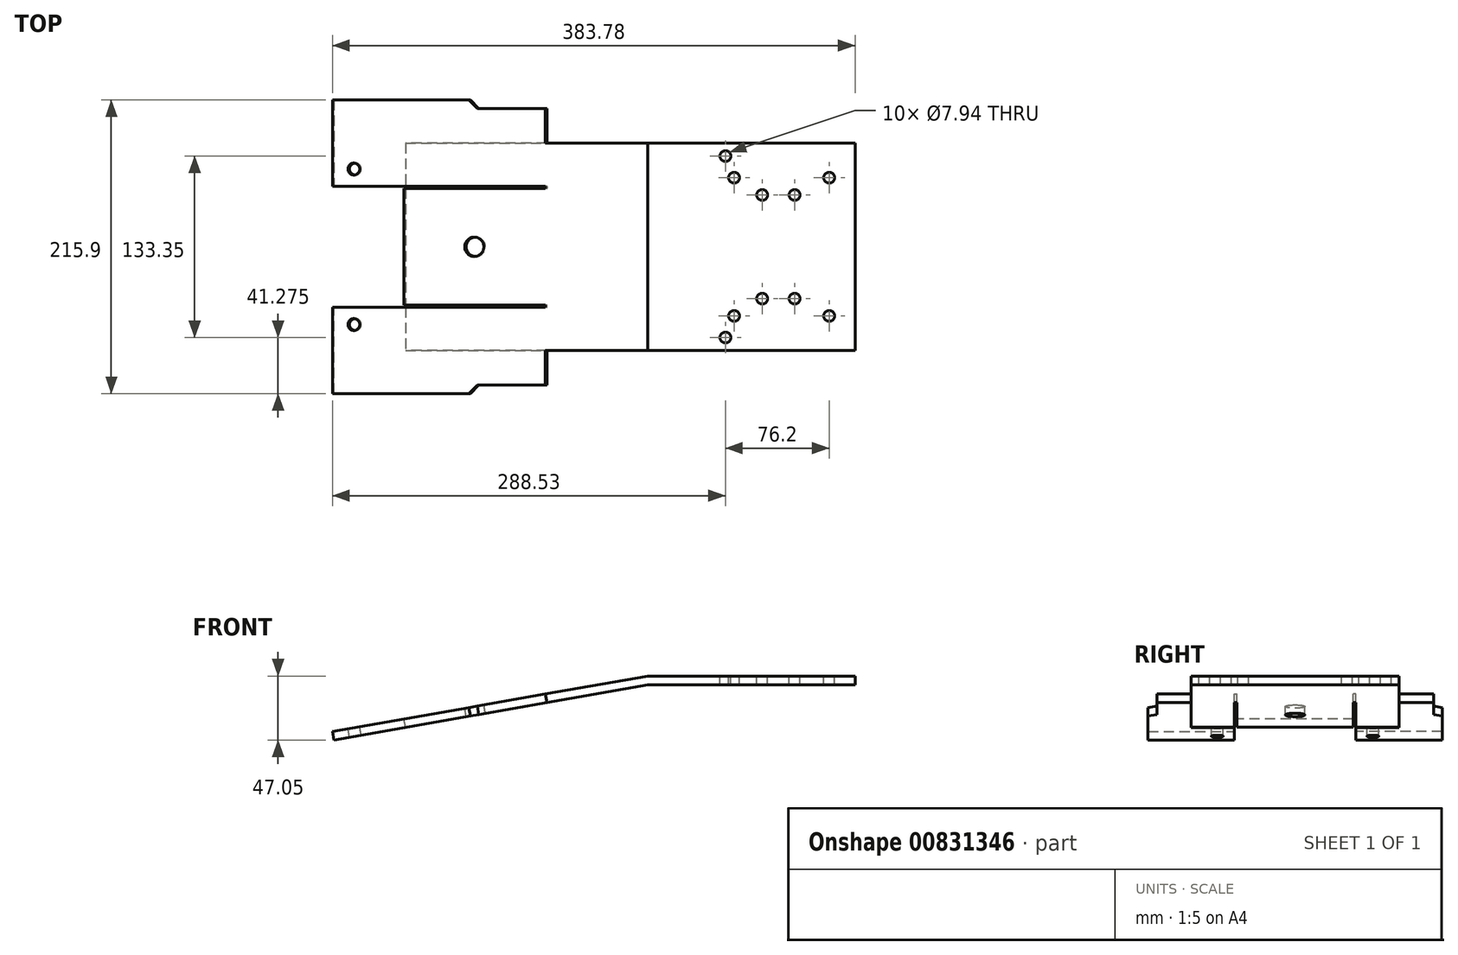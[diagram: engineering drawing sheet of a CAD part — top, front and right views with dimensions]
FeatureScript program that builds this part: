
annotation { "Feature Type Name" : "Feature", "Feature Type Description" : "" }
export const myFeature = defineFeature(function(context is Context, id is Id, definition is map)
    precondition{}
    {
        {
            var Q0;
            Q0=qCreatedBy(makeId("Front.planeOp"),FACE);
            var sketch = newSketch(context, id + "F0", { "sketchPlane" : qUnion([Q0])});
            skLineSegment(sketch, "E0", {"start": v(0, 0) * mm, "end": v(-152.4, 0) * mm});
            skLineSegment(sketch, "E1", {"start": v(-152.4, 0) * mm, "end": v(-330.2, -31.35) * mm});
            skLineSegment(sketch, "E2", {"start": v(-330.2, -31.35) * mm, "end": v(-331.29, -25.2) * mm});
            skLineSegment(sketch, "E3", {"start": v(-331.29, -25.2) * mm, "end": v(-152.4, 6.35) * mm});
            skLineSegment(sketch, "E4", {"start": v(-152.4, 6.35) * mm, "end": v(0, 6.35) * mm});
            skLineSegment(sketch, "E5", {"start": v(0, 6.35) * mm, "end": v(0, 0) * mm});
            skSolve(sketch);
        }
        {
            var Q0;
            Q0 = qSketchRegion(id + "F0", true);
            extrude(context, id + "F1", {"entities" : qUnion([Q0]), "oppositeDirection" : true, "depth" : 152.4 * mm, "offsetDistance" : 25.4 * mm});
        }
        {
            var Q0;
            Q0=makeQuery(id+"F1.opExtrude","SWEPT_FACE",FACE,{"disambiguationData":[OSD([sQuery(id+"F0.wireOp",EDGE,"E3")])]});
            var sketch = newSketch(context, id + "F2", { "sketchPlane" : qUnion([Q0])});
            skCircle(sketch, "E6", {"center": v(-278.24, 76.2) * mm, "radius": 7.14 * mm});
            skPoint(sketch, "E6.centerSnap0", {"position": v(-330.63, 76.2) * mm});
            skSolve(sketch);
        }
        {
            var Q0;
            Q0 = qSketchRegion(id + "F2", true);
            extrude(context, id + "F3", {"entities" : qUnion([Q0]), "operationType" : NewBodyOperationType.REMOVE, "endBound" : BoundingType.THROUGH_ALL, "oppositeDirection" : true, "depth" : 25.4 * mm, "offsetDistance" : 25.4 * mm});
        }
        {
            var Q0;
            Q0=makeQuery(id+"F1.opExtrude","SWEPT_FACE",FACE,{"disambiguationData":[OSD([sQuery(id+"F0.wireOp",EDGE,"E4")])]});
            var sketch = newSketch(context, id + "F4", { "sketchPlane" : qUnion([Q0])});
            skCircle(sketch, "E7", {"center": v(-19.05, 127) * mm, "radius": 3.97 * mm});
            skCircle(sketch, "E8", {"center": v(-19.05, 25.4) * mm, "radius": 3.97 * mm});
            skCircle(sketch, "E9", {"center": v(-88.9, 25.4) * mm, "radius": 3.97 * mm});
            skCircle(sketch, "E10", {"center": v(-88.9, 127) * mm, "radius": 3.97 * mm});
            skCircle(sketch, "E11", {"center": v(-95.25, 9.53) * mm, "radius": 3.97 * mm});
            skCircle(sketch, "E12", {"center": v(-95.25, 142.88) * mm, "radius": 3.97 * mm});
            skCircle(sketch, "E13", {"center": v(-68.26, 114.3) * mm, "radius": 3.97 * mm});
            skCircle(sketch, "E14", {"center": v(-44.45, 114.3) * mm, "radius": 3.97 * mm});
            skCircle(sketch, "E15", {"center": v(-68.26, 38.1) * mm, "radius": 3.97 * mm});
            skCircle(sketch, "E16", {"center": v(-44.45, 38.1) * mm, "radius": 3.97 * mm});
            skSolve(sketch);
        }
        {
            var Q0;
            Q0 = qSketchRegion(id + "F4", true);
            extrude(context, id + "F5", {"entities" : qUnion([Q0]), "operationType" : NewBodyOperationType.REMOVE, "endBound" : BoundingType.THROUGH_ALL, "oppositeDirection" : true, "depth" : 25.4 * mm, "offsetDistance" : 25.4 * mm});
        }
        {
            var Q0;
            Q0=makeQuery(id+"F1.opExtrude","SWEPT_FACE",FACE,{"disambiguationData":[OSD([sQuery(id+"F0.wireOp",EDGE,"E3")])]});
            var sketch = newSketch(context, id + "F6", { "sketchPlane" : qUnion([Q0])});
            skLineSegment(sketch, "E17.0", {"start": v(-330.63, 152.4) * mm, "end": v(-225.18, 152.4) * mm});
            skLineSegment(sketch, "E17.1", {"start": v(-330.63, 152.4) * mm, "end": v(-330.63, 120.65) * mm});
            skLineSegment(sketch, "E18.0", {"start": v(-383.93, 184.15) * mm, "end": v(-282.33, 184.15) * mm});
            skLineSegment(sketch, "E19.0", {"start": v(-383.93, 120.65) * mm, "end": v(-330.63, 120.65) * mm});
            skLineSegment(sketch, "E20.0", {"start": v(-148.98, 152.4) * mm, "end": v(-148.98, 0) * mm});
            skLineSegment(sketch, "E21.0", {"start": v(-225.18, 177.8) * mm, "end": v(-225.18, 152.4) * mm});
            skLineSegment(sketch, "E22.0", {"start": v(-383.93, 184.15) * mm, "end": v(-383.93, 120.65) * mm});
            skLineSegment(sketch, "E23.0", {"start": v(-275.98, 177.8) * mm, "end": v(-225.18, 177.8) * mm});
            skLineSegment(sketch, "E24", {"start": v(-282.33, 184.15) * mm, "end": v(-275.98, 177.8) * mm});
            skLineSegment(sketch, "E25", {"start": v(-278.24, 76.2) * mm, "end": v(-330.63, 76.2) * mm});
            skLineSegment(sketch, "E26.MirrorCS", {"start": v(-282.33, -31.75) * mm, "end": v(-275.98, -25.4) * mm});
            skLineSegment(sketch, "E27.MirrorCS", {"start": v(-383.93, 31.75) * mm, "end": v(-330.63, 31.75) * mm});
            skLineSegment(sketch, "E28.MirrorCS", {"start": v(-225.18, -25.4) * mm, "end": v(-225.18, 0) * mm});
            skLineSegment(sketch, "E29.MirrorCS", {"start": v(-275.98, -25.4) * mm, "end": v(-225.18, -25.4) * mm});
            skLineSegment(sketch, "E30.MirrorCS", {"start": v(-330.63, 0) * mm, "end": v(-330.63, 31.75) * mm});
            skLineSegment(sketch, "E31.MirrorCS", {"start": v(-383.93, -31.75) * mm, "end": v(-383.93, 31.75) * mm});
            skLineSegment(sketch, "E32.MirrorCS", {"start": v(-383.93, -31.75) * mm, "end": v(-282.33, -31.75) * mm});
            skLineSegment(sketch, "E33.MirrorCS", {"start": v(-330.63, 0) * mm, "end": v(-225.18, 0) * mm});
            skSolve(sketch);
        }
        {
            var Q0;
            Q0 = qSketchRegion(id + "F6", true);
            extrude(context, id + "F7", {"entities" : qUnion([Q0]), "operationType" : NewBodyOperationType.ADD, "oppositeDirection" : true, "depth" : 6.35 * mm, "offsetDistance" : 25.4 * mm});
        }
        {
            var Q0;
            Q0=makeQuery(id+"F7.boolean.opBoolean","MERGE",FACE,{"derivedFrom":[makeQuery(id+"F1.opExtrude","SWEPT_FACE",FACE,{"disambiguationData":[OSD([sQuery(id+"F0.wireOp",EDGE,"E3")])]}),makeQuery(id+"F7.opExtrude","CAP_FACE",FACE,{"disambiguationData":[OSD([sQuery(id+"F6.wireOp",EDGE,"E17.0"),sQuery(id+"F6.wireOp",EDGE,"E17.1"),sQuery(id+"F6.wireOp",EDGE,"E18.0"),sQuery(id+"F6.wireOp",EDGE,"E19.0"),sQuery(id+"F6.wireOp",EDGE,"E21.0"),sQuery(id+"F6.wireOp",EDGE,"E22.0"),sQuery(id+"F6.wireOp",EDGE,"E23.0"),sQuery(id+"F6.wireOp",EDGE,"E24")])],"isStart":true}),makeQuery(id+"F7.opExtrude","CAP_FACE",FACE,{"disambiguationData":[OSD([sQuery(id+"F6.wireOp",EDGE,"E26.MirrorCS"),sQuery(id+"F6.wireOp",EDGE,"E27.MirrorCS"),sQuery(id+"F6.wireOp",EDGE,"E28.MirrorCS"),sQuery(id+"F6.wireOp",EDGE,"E29.MirrorCS"),sQuery(id+"F6.wireOp",EDGE,"E30.MirrorCS"),sQuery(id+"F6.wireOp",EDGE,"E31.MirrorCS"),sQuery(id+"F6.wireOp",EDGE,"E32.MirrorCS"),sQuery(id+"F6.wireOp",EDGE,"E33.MirrorCS")])],"isStart":true})]});
            var sketch = newSketch(context, id + "F8", { "sketchPlane" : qUnion([Q0])});
            skPoint(sketch, "E34.endSnap0", {"position": v(-357.28, 31.75) * mm});
            skLineSegment(sketch, "E35.0", {"start": v(-383.93, 184.15) * mm, "end": v(-383.93, 120.65) * mm});
            skLineSegment(sketch, "E35.3", {"start": v(-383.93, -31.75) * mm, "end": v(-383.93, 31.75) * mm});
            skCircle(sketch, "E36", {"center": v(-368.06, 133.35) * mm, "radius": 4.37 * mm});
            skCircle(sketch, "E37", {"center": v(-368.06, 19.05) * mm, "radius": 4.37 * mm});
            skLineSegment(sketch, "E38", {"start": v(-383.93, 120.65) * mm, "end": v(-225.18, 120.65) * mm});
            skLineSegment(sketch, "E39", {"start": v(-383.93, 31.75) * mm, "end": v(-225.18, 31.75) * mm});
            skLineSegment(sketch, "E40.0", {"start": v(-383.93, 119.06) * mm, "end": v(-225.18, 119.06) * mm});
            skLineSegment(sketch, "E41.0", {"start": v(-383.93, 33.34) * mm, "end": v(-225.18, 33.34) * mm});
            skLineSegment(sketch, "E42", {"start": v(-225.18, 120.65) * mm, "end": v(-225.18, 119.06) * mm});
            skLineSegment(sketch, "E43", {"start": v(-225.18, 31.75) * mm, "end": v(-225.18, 33.34) * mm});
            skLineSegment(sketch, "E44", {"start": v(-330.63, 120.65) * mm, "end": v(-330.63, 119.06) * mm});
            skLineSegment(sketch, "E45", {"start": v(-330.63, 31.75) * mm, "end": v(-330.63, 33.34) * mm});
            skSolve(sketch);
        }
        {
            var Q0;
            Q0 = qSketchRegion(id + "F8", true);
            extrude(context, id + "F9", {"entities" : qUnion([Q0]), "operationType" : NewBodyOperationType.REMOVE, "endBound" : BoundingType.THROUGH_ALL, "oppositeDirection" : true, "depth" : 25.4 * mm, "offsetDistance" : 25.4 * mm});
        }
    });
